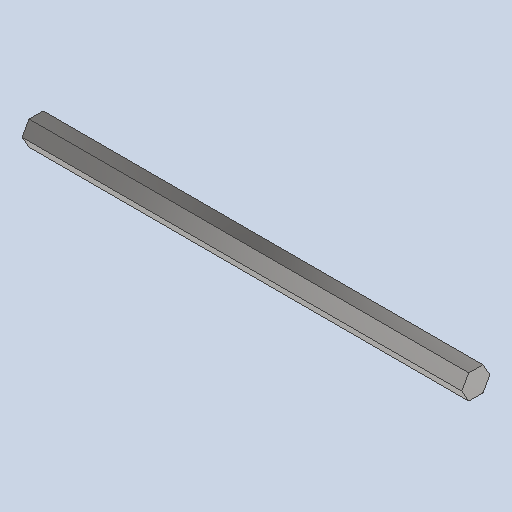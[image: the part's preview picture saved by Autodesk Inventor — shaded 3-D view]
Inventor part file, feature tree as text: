
AUTODESK INVENTOR PART (.ipt)
format: ipt  version: 2023 (Build 270158000, 158)  size: 91,648 bytes
history: native  units: in
note: dims shown in document units (in); Inventor stores cm internally (conversion verified against a paired STEP export)
features: other x3, sketch x1
ambient origin geometry x8: Origin, YZ Plane, XZ Plane, XY Plane, X Axis, Y Axis, Z Axis, Center Point
bodies: Solid1 (feature_tree)
feature tree (4):
  other  "9in-0.5inHexAxel.ipt"
  other  "Solid1::9in-0.5inHexAxel.ipt"
  other  "TaggingFeature1"
  sketch  "Sketch1"  dims[d0=0.3937in]
